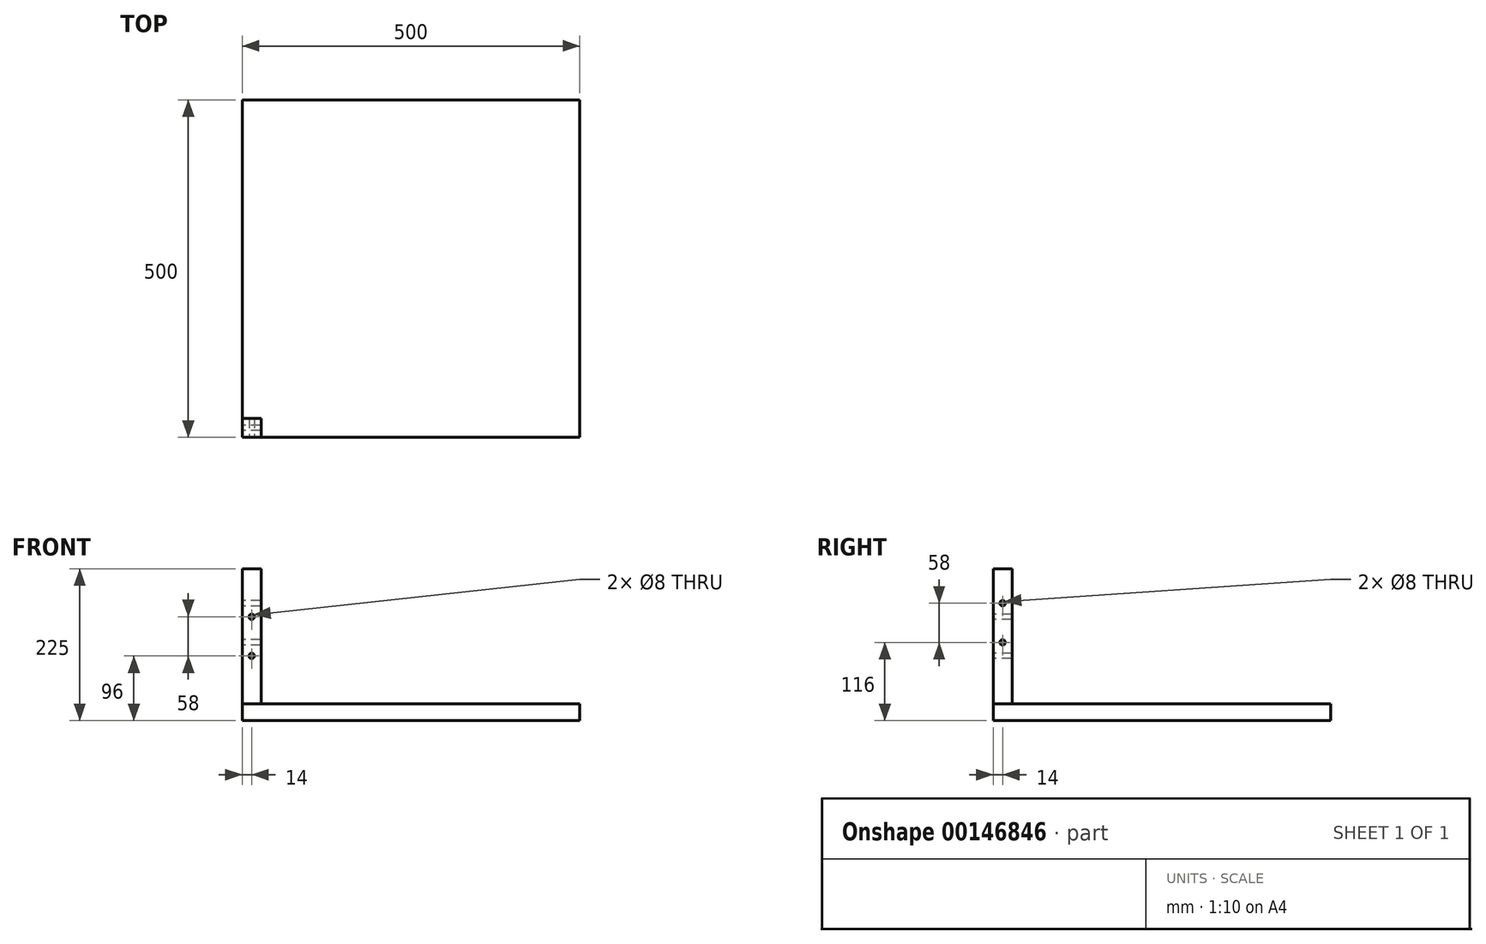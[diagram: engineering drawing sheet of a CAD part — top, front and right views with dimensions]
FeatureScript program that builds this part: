
annotation { "Feature Type Name" : "Feature", "Feature Type Description" : "" }
export const myFeature = defineFeature(function(context is Context, id is Id, definition is map)
    precondition{}
    {
        {
            var Q0;
            Q0=qCreatedBy(makeId("Top.planeOp"),FACE);
            var sketch = newSketch(context, id + "F0", { "sketchPlane" : qUnion([Q0])});
            skLineSegment(sketch, "E0.bottom", {"start": v(0, 0) * mm, "end": v(500, 0) * mm});
            skLineSegment(sketch, "E0.top", {"start": v(0, 500) * mm, "end": v(500, 500) * mm});
            skLineSegment(sketch, "E0.left", {"start": v(0, 0) * mm, "end": v(0, 500) * mm});
            skLineSegment(sketch, "E0.right", {"start": v(500, 0) * mm, "end": v(500, 500) * mm});
            skSolve(sketch);
        }
        {
            var Q0;
            Q0=qSketchRegion(id+"F0",true);
            extrude(context, id + "F1", {"entities" : qUnion([Q0]), "oppositeDirection" : true, "depth" : 25 * mm});
        }
        {
            var Q0;
            Q0=qCreatedBy(makeId("Top.planeOp"),FACE);
            var sketch = newSketch(context, id + "F2", { "sketchPlane" : qUnion([Q0])});
            skLineSegment(sketch, "E1.bottom", {"start": v(0, 0) * mm, "end": v(28, 0) * mm});
            skLineSegment(sketch, "E1.top", {"start": v(0, 28) * mm, "end": v(28, 28) * mm});
            skLineSegment(sketch, "E1.left", {"start": v(0, 0) * mm, "end": v(0, 28) * mm});
            skLineSegment(sketch, "E1.right", {"start": v(28, 0) * mm, "end": v(28, 28) * mm});
            skSolve(sketch);
        }
        {
            var Q0;
            Q0=qSketchRegion(id+"F2",true);
            extrude(context, id + "F3", {"entities" : qUnion([Q0]), "depth" : 200 * mm});
        }
        {
            var Q0;
            Q0=makeQuery(id+"F3.opExtrude","SWEPT_FACE",FACE,{"disambiguationData":[OSD([sQuery(id+"F2.wireOp",EDGE,"E1.bottom")])]});
            var sketch = newSketch(context, id + "F4", { "sketchPlane" : qUnion([Q0])});
            skCircle(sketch, "E2", {"center": v(14, 129) * mm, "radius": 4 * mm});
            skCircle(sketch, "E3", {"center": v(14, 71) * mm, "radius": 4 * mm});
            skLineSegment(sketch, "E4", {"start": v(14, 0) * mm, "end": v(14, 200) * mm, "construction": true});
            skSolve(sketch);
        }
        {
            var Q0;
            Q0=qSketchRegion(id+"F4",true);
            extrude(context, id + "F5", {"entities" : qUnion([Q0]), "operationType" : NewBodyOperationType.REMOVE, "oppositeDirection" : true, "depth" : 30 * mm});
        }
        {
            var Q0;
            Q0=makeQuery(id+"F3.opExtrude","SWEPT_FACE",FACE,{"disambiguationData":[OSD([sQuery(id+"F2.wireOp",EDGE,"E1.left")])]});
            var sketch = newSketch(context, id + "F6", { "sketchPlane" : qUnion([Q0])});
            skLineSegment(sketch, "E5", {"start": v(-14, 200) * mm, "end": v(-14, 0) * mm, "construction": true});
            skCircle(sketch, "E6", {"center": v(-14, 149) * mm, "radius": 4 * mm});
            skCircle(sketch, "E7", {"center": v(-14, 91) * mm, "radius": 4 * mm});
            skSolve(sketch);
        }
        {
            var Q0;
            Q0=qSketchRegion(id+"F6",true);
            extrude(context, id + "F7", {"entities" : qUnion([Q0]), "operationType" : NewBodyOperationType.REMOVE, "oppositeDirection" : true, "depth" : 30 * mm});
        }
    });
